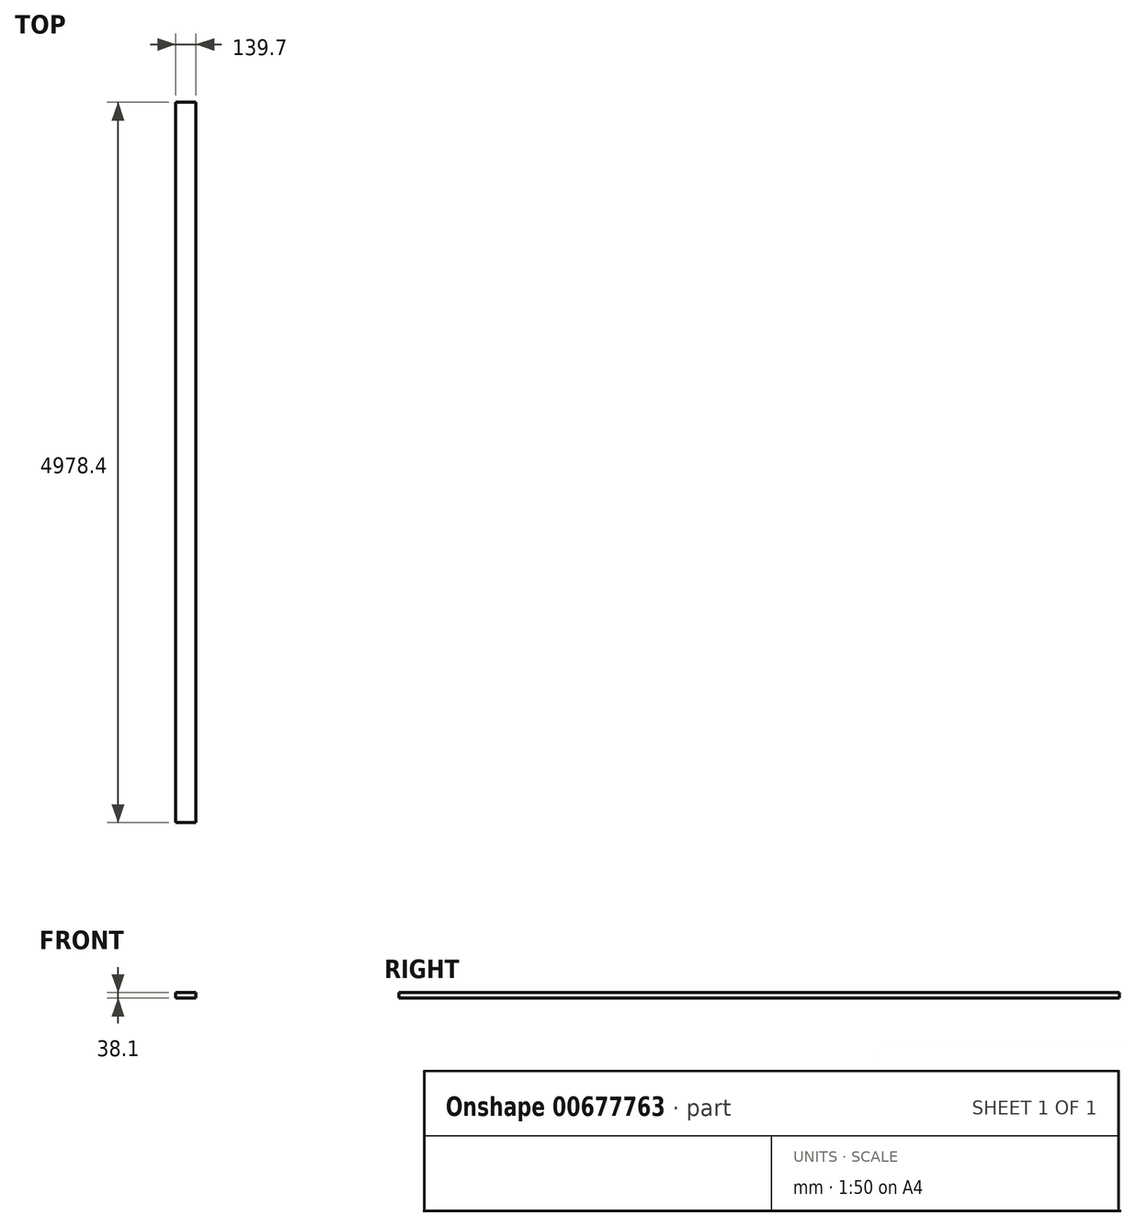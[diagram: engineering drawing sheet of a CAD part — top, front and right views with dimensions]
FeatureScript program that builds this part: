
annotation { "Feature Type Name" : "Feature", "Feature Type Description" : "" }
export const myFeature = defineFeature(function(context is Context, id is Id, definition is map)
    precondition{}
    {
        {
            var Q0;
            Q0=qCreatedBy(makeId("Front.planeOp"),FACE);
            var sketch = newSketch(context, id + "F0", { "sketchPlane" : qUnion([Q0])});
            skLineSegment(sketch, "E0.bottom", {"start": v(-696.78, -75.97) * mm, "end": v(-836.48, -75.97) * mm});
            skLineSegment(sketch, "E0.top", {"start": v(-696.78, -114.07) * mm, "end": v(-836.48, -114.07) * mm});
            skLineSegment(sketch, "E0.left", {"start": v(-696.78, -75.97) * mm, "end": v(-696.78, -114.07) * mm});
            skLineSegment(sketch, "E0.right", {"start": v(-836.48, -75.97) * mm, "end": v(-836.48, -114.07) * mm});
            skSolve(sketch);
        }
        {
            var Q0;
            Q0=makeQuery(id+"F0.imprint","IMPRINT",FACE,{"disambiguationData":[TD([[makeQuery(id+"F0.imprint","IMPRINT",EDGE,{"derivedFrom":sQuery(id+"F0.wireOp",EDGE,"E0.bottom")}),1.0]])]});
            extrude(context, id + "F1", {"entities" : qUnion([Q0]), "depth" : 4978.4 * mm, "offsetDistance" : 25.4 * mm});
        }
    });
